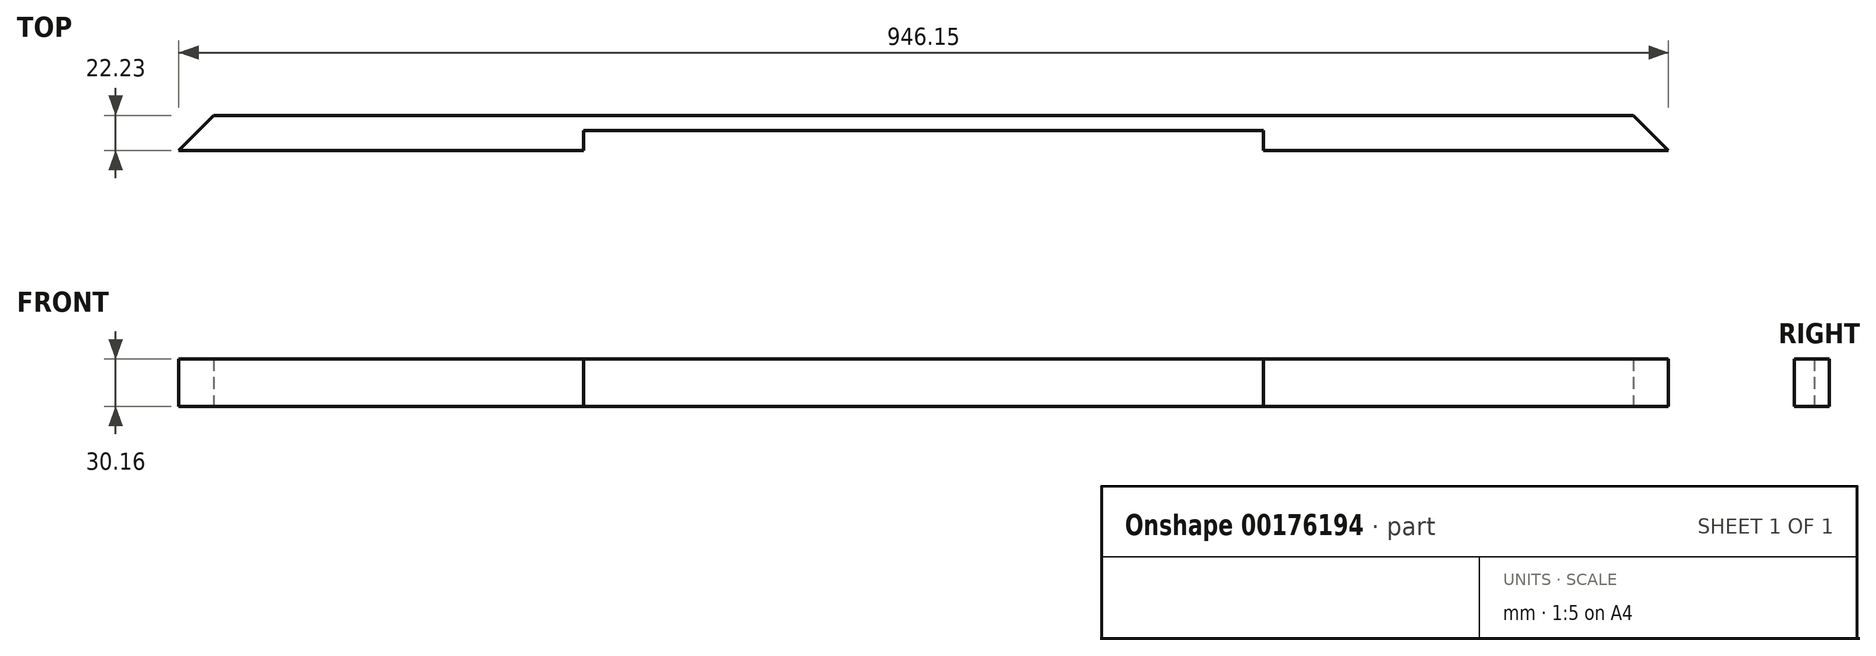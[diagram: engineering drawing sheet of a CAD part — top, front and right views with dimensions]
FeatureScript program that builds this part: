
annotation { "Feature Type Name" : "Feature", "Feature Type Description" : "" }
export const myFeature = defineFeature(function(context is Context, id is Id, definition is map)
    precondition{}
    {
        {
            var Q0;
            Q0=qCreatedBy(makeId("Top.planeOp"),FACE);
            var sketch = newSketch(context, id + "F0", { "sketchPlane" : qUnion([Q0])});
            skLineSegment(sketch, "E0.bottom", {"start": v(0, 0) * mm, "end": v(946.15, 0) * mm});
            skLineSegment(sketch, "E0.top", {"start": v(22.22, 22.23) * mm, "end": v(923.92, 22.23) * mm});
            skLineSegment(sketch, "E1", {"start": v(0, 0) * mm, "end": v(22.22, 22.22) * mm});
            skLineSegment(sketch, "E2", {"start": v(946.15, 0) * mm, "end": v(923.92, 22.22) * mm});
            skSolve(sketch);
        }
        {
            var Q0;
            Q0=makeQuery(id+"F0.imprint","IMPRINT",FACE,{"disambiguationData":[TD([[makeQuery(id+"F0.imprint","IMPRINT",EDGE,{"derivedFrom":sQuery(id+"F0.wireOp",EDGE,"E0.bottom")}),1.0]])]});
            extrude(context, id + "F1", {"entities" : qUnion([Q0]), "depth" : 30.16 * mm});
        }
        {
            var Q0;
            Q0=makeQuery(id+"F1.opExtrude","SWEPT_FACE",FACE,{"disambiguationData":[OSD([sQuery(id+"F0.wireOp",EDGE,"E0.bottom")])]});
            var sketch = newSketch(context, id + "F2", { "sketchPlane" : qUnion([Q0])});
            skLineSegment(sketch, "E3.bottom", {"start": v(688.98, 30.16) * mm, "end": v(257.18, 30.16) * mm});
            skLineSegment(sketch, "E3.top", {"start": v(688.98, 0) * mm, "end": v(257.18, 0) * mm});
            skLineSegment(sketch, "E3.left", {"start": v(688.98, 30.16) * mm, "end": v(688.98, 0) * mm});
            skLineSegment(sketch, "E3.right", {"start": v(257.18, 30.16) * mm, "end": v(257.18, 0) * mm});
            skPoint(sketch, "E3.middle", {"position": v(473.08, 15.08) * mm});
            skPoint(sketch, "E3.middle.positionSnap0", {"position": v(473.08, 30.16) * mm});
            skPoint(sketch, "E3.centerSnap0", {"position": v(473.08, 30.16) * mm});
            skSolve(sketch);
        }
        {
            var Q0;
            Q0=makeQuery(id+"F2.imprint","IMPRINT",FACE,{"disambiguationData":[TD([[makeQuery(id+"F2.imprint","IMPRINT",EDGE,{"derivedFrom":sQuery(id+"F2.wireOp",EDGE,"E3.bottom")}),-1.0]])]});
            extrude(context, id + "F3", {"entities" : qUnion([Q0]), "operationType" : NewBodyOperationType.REMOVE, "oppositeDirection" : true, "depth" : 12.7 * mm});
        }
    });
